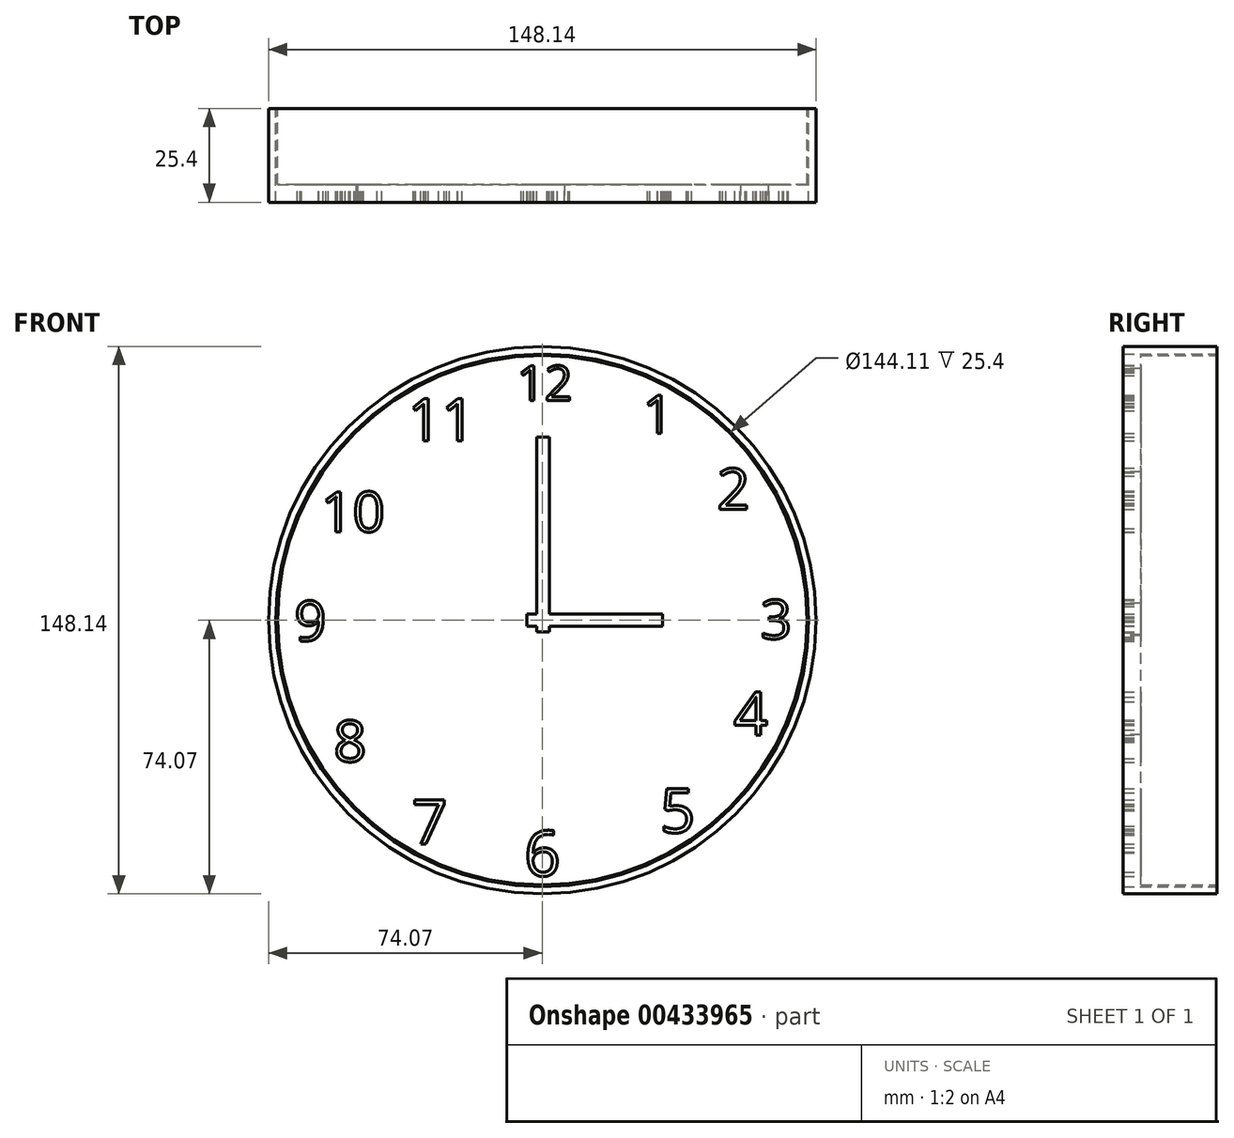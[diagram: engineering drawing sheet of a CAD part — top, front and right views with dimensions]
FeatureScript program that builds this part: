
annotation { "Feature Type Name" : "Feature", "Feature Type Description" : "" }
export const myFeature = defineFeature(function(context is Context, id is Id, definition is map)
    precondition{}
    {
        {
            var Q0;
            Q0=qCreatedBy(makeId("Front.planeOp"),FACE);
            var sketch = newSketch(context, id + "F0", { "sketchPlane" : qUnion([Q0])});
            skCircle(sketch, "E0", {"center": v(0, 0) * mm, "radius": 74.07 * mm});
            skCircle(sketch, "E1", {"center": v(0, 0) * mm, "radius": 72.06 * mm});
            skSolve(sketch);
        }
        {
            var Q0;
            Q0 = qSketchRegion(id + "F0", true);
            extrude(context, id + "F1", {"entities" : qUnion([Q0]), "depth" : 25.4 * mm});
        }
        {
            var Q0;
            Q0=qCreatedBy(makeId("Front.planeOp"),FACE);
            var sketch = newSketch(context, id + "F2", { "sketchPlane" : qUnion([Q0])});
            skCircle(sketch, "E2", {"center": v(0, 0) * mm, "radius": 71.63 * mm});
            skSolve(sketch);
        }
        {
            var Q0;
            Q0 = qSketchRegion(id + "F2", true);
            extrude(context, id + "F3", {"entities" : qUnion([Q0]), "depth" : 20.57 * mm});
        }
        {
            var Q0;
            Q0=qCreatedBy(makeId("Front.planeOp"),FACE);
            var sketch = newSketch(context, id + "F4", { "sketchPlane" : qUnion([Q0])});
            skText(sketch, "E3", { "text": "12\n", "fontName": "OpenSans-Regular.ttf"});
            skText(sketch, "E4", { "text": "1", "fontName": "OpenSans-Regular.ttf"});
            skText(sketch, "E5", { "text": "2", "fontName": "OpenSans-Regular.ttf"});
            skText(sketch, "E6", { "text": "3\n", "fontName": "OpenSans-Regular.ttf"});
            skText(sketch, "E7", { "text": "4", "fontName": "OpenSans-Regular.ttf"});
            skText(sketch, "E8", { "text": "5", "fontName": "OpenSans-Regular.ttf"});
            skText(sketch, "E9", { "text": "7", "fontName": "OpenSans-Regular.ttf"});
            skText(sketch, "E10", { "text": "8", "fontName": "OpenSans-Regular.ttf"});
            skText(sketch, "E11", { "text": "9", "fontName": "OpenSans-Regular.ttf"});
            skText(sketch, "E12", { "text": "10", "fontName": "OpenSans-Regular.ttf"});
            skText(sketch, "E13", { "text": "11", "fontName": "OpenSans-Regular.ttf"});
            skText(sketch, "E14", { "text": "6", "fontName": "OpenSans-Regular.ttf"});
            const initialGuessF4  = {"E3": [-0.00688, 0.05946, 1, 0, 0.00946], "E4": [0.02722, 0.05058, 1, 0, 0.01032], "E5": [0.04728, 0.02995, 1, 0, 0.01118], "E6": [0.05903, -0.00501, 1, 0, 0.0106], "E7": [0.0518, -0.0311, 1, 0, 0.01175], "E8": [0.0318, -0.05746, 1, 0, 0.01204], "E9": [-0.03525, -0.0606, 1, 0, 0.01204], "E10": [-0.05645, -0.03826, 1, 0, 0.01118], "E11": [-0.06706, -0.00559, 1, 0, 0.01089], "E12": [-0.0599, 0.02393, 1, 0, 0.01089], "E13": [-0.0364, 0.04857, 1, 0, 0.01146], "E14": [-0.00487, -0.0692, 1, 0, 0.01232]};
            skSetInitialGuess(sketch, initialGuessF4);
            skSolve(sketch);
        }
        {
            var Q0;
            Q0 = qSketchRegion(id + "F4", true);
            extrude(context, id + "F5", {"entities" : qUnion([Q0]), "operationType" : NewBodyOperationType.ADD, "depth" : 25.4 * mm});
        }
        {
            var Q0;
            Q0=qCreatedBy(makeId("Front.planeOp"),FACE);
            var sketch = newSketch(context, id + "F6", { "sketchPlane" : qUnion([Q0])});
            skLineSegment(sketch, "E15.bottom", {"start": v(-1.54, -3.19) * mm, "end": v(1.98, -3.19) * mm});
            skLineSegment(sketch, "E15.top", {"start": v(-1.54, 49.6) * mm, "end": v(1.98, 49.6) * mm});
            skLineSegment(sketch, "E15.left", {"start": v(-1.54, -3.19) * mm, "end": v(-1.54, 49.6) * mm});
            skLineSegment(sketch, "E15.right", {"start": v(1.98, -3.19) * mm, "end": v(1.98, 49.6) * mm});
            skLineSegment(sketch, "E16.bottom", {"start": v(-4.22, 1.64) * mm, "end": v(32.52, 1.64) * mm});
            skLineSegment(sketch, "E16.top", {"start": v(-4.22, -1.66) * mm, "end": v(32.52, -1.66) * mm});
            skLineSegment(sketch, "E16.left", {"start": v(-4.22, 1.64) * mm, "end": v(-4.22, -1.66) * mm});
            skLineSegment(sketch, "E16.right", {"start": v(32.52, 1.64) * mm, "end": v(32.52, -1.66) * mm});
            skSolve(sketch);
        }
        {
            var Q0;
            Q0 = qSketchRegion(id + "F6", true);
            extrude(context, id + "F7", {"entities" : qUnion([Q0]), "operationType" : NewBodyOperationType.ADD, "depth" : 25.4 * mm});
        }
    });
